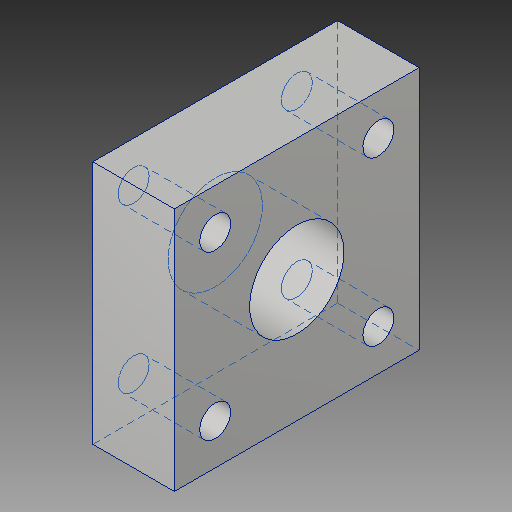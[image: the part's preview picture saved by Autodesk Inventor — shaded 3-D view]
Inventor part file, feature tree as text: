
AUTODESK INVENTOR PART (.ipt)
format: ipt  version: 2019 (Build 230136000, 136)  size: 116,736 bytes
history: native  units: in
note: dims shown in document units (in); Inventor stores cm internally (conversion verified against a paired STEP export)
features: extrude x1, sketch x1
ambient origin geometry x8: Origin, YZ Plane, XZ Plane, XY Plane, X Axis, Y Axis, Z Axis, Center Point
bodies: Solid1 (feature_tree)
feature tree (2):
  extrude  "Extrusion1"  Depth=0.5in
  sketch  "Sketch1"  dims[d0=1.5in d1=0.5781in d2=0.19in d3=1.0in d4=0.5in d5=0.0in]
